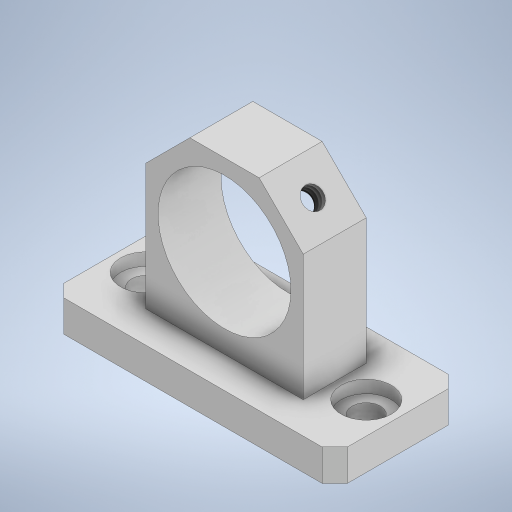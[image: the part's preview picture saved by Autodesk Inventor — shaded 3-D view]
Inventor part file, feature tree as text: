
AUTODESK INVENTOR PART (.ipt)
format: ipt  version: 2024.2 (Build 282272000, 272)  size: 393,216 bytes
history: native  units: in
note: dims shown in document units (in); Inventor stores cm internally (conversion verified against a paired STEP export)
features: sketch x8, extrude x6, chamfer x2, hole x2
ambient origin geometry x8: Origin, YZ Plane, XZ Plane, XY Plane, X Axis, Y Axis, Z Axis, Center Point
bodies: Solid1 (feature_tree)
feature tree (18):
  extrude  "Extrusion1"  Depth=0.7874in
  extrude  "Extrusion2"  Depth=0.9843in
  extrude  "Extrusion3"  Depth=0.3937in TaperAngle=0.0deg
  chamfer  "Chamfer1"  Distance=1.1811in
  hole  "Hole1"  [1 undecoded]
  hole  "Hole2"  [1 undecoded]
  extrude  "Extrusion8"  Depth=0.0787in
  extrude  "Extrusion9"  Depth=0.0787in
  extrude  "Extrusion10"  Depth=0.0787in TaperAngle=0.0deg
  chamfer  "Chamfer3"  Distance=0.1772in
  sketch  "Sketch2"  dims[d0=1.7717in d1=0.7874in]
  sketch  "Sketch3"  dims[d2=0.1969in d3=0.0in d4=0.9843in]
  sketch  "Sketch4"  dims[d5=0.3937in d6=1.063in d7=0.0in]
  sketch  "Sketch6"  dims[d8=0.5531in]
  sketch  "Sketch7"  dims[d9=0.8307in d10=1.1811in d11=0.0in]
  sketch  "Sketch13"  dims[d12=0.2756in d13=0.0787in d14=45.0deg]
  sketch  "Sketch14"  dims[d15=0.13in d16=0.328in d17=0.1575in d18=0.0787in d19=90.0deg d20=0.4843in d21=0.0in]
  sketch  "Sketch15"  dims[d22=0.13in d23=0.328in d24=0.1575in d25=0.0787in d26=90.0deg d27=0.4843in d28=0.0in d69=0.1969in d70=0.1969in d71=0.315in d72=0.315in d73=0.0787in d74=0.0in d75=0.1772in d76=0.0in d77=0.0in d78=0.1969in d79=0.1772in d80=0.0791in d81=0.0791in d82=0.0394in d83=0.0791in d84=0.0827in d85=0.0in d86=0.0787in d87=0.0787in d88=45.0deg]
note: 2 required parameter values undecoded (feature->parameter linkage not recoverable at this tier; creation-order binding heuristic only, values carry confidence <= 0.55)
